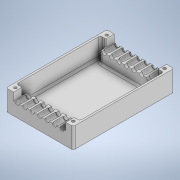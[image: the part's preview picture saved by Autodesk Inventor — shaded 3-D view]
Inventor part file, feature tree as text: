
AUTODESK INVENTOR PART (.ipt)
format: ipt  version: 2021 (Build 250183000, 183)  size: 422,400 bytes
history: native  units: mm
features: extrude x8, sketch x8, fillet x5
ambient origin geometry x8: Origin, YZ Plane, XZ Plane, XY Plane, X Axis, Y Axis, Z Axis, Center Point
bodies: Body1 (feature_tree)
feature tree (21):
  extrude  "Extrusion20"  Depth=2.0mm
  extrude  "Extrusion21"  Depth=2.0mm TaperAngle=0.0deg
  extrude  "Extrusion24"  Depth=2.0mm TaperAngle=0.0deg
  fillet  "Fillet12"  Radius=3.0mm
  extrude  "Extrusion25"  Depth=3.0mm
  fillet  "Fillet13"  Radius=3.0mm
  extrude  "Extrusion26"  Depth=2.0mm
  extrude  "Extrusion27"  Depth=56.0mm
  extrude  "Extrusion28"  Depth=15.0mm
  extrude  "Extrusion29"  Depth=2.0mm
  fillet  "Fillet14"  Radius=8.0mm
  fillet  "Fillet15"  Radius=2.0mm
  fillet  "Fillet16"  Radius=56.0mm
  sketch  "Sketch26"  dims[d181=2.0mm d182=2.0mm d184=2.0mm d186=2.0mm d187=8.0mm d190=8.0mm d193=8.0mm d196=8.0mm d249=108.0mm]
  sketch  "Sketch27"  dims[d250=72.0mm d251=2.0mm d252=0.0mm]
  sketch  "Sketch30"  dims[d253=2.0mm d254=20.0mm d255=0.0mm d292=3.0mm]
  sketch  "Sketch31"  dims[d293=3.0mm d294=3.0mm d295=3.0mm]
  sketch  "Sketch32"  dims[d296=20.0mm d297=0.0mm d298=2.0mm]
  sketch  "Sketch33"  dims[d299=56.0mm d300=56.0mm]
  sketch  "Sketch34"  dims[d301=8.0mm d302=15.0mm]
  sketch  "Sketch35"  dims[d303=8.0mm d304=15.0mm d305=8.0mm d306=0.0mm d307=2.0mm d308=56.0mm d309=15.0mm d310=15.0mm d311=12.0mm d312=0.0mm d313=6.0mm d314=4.0mm d315=70.0mm d317=8.0mm d318=10.0mm d320=10.0mm d322=1000.0mm d323=0.0mm d324=1.0mm d325=1.0mm d326=3.0mm d327=3.0mm d328=8.0mm d329=0.0mm d330=4.0mm d331=4.5mm d332=70.0mm d334=8.0mm d335=10.0mm d337=10.0mm d339=1000.0mm d340=0.0mm d341=2.0mm d342=2.0mm d343=2.0mm d344=5.0mm d345=5.0mm d346=5.0mm d347=5.0mm d348=5.0mm d349=5.0mm d350=5.0mm d351=5.0mm]
